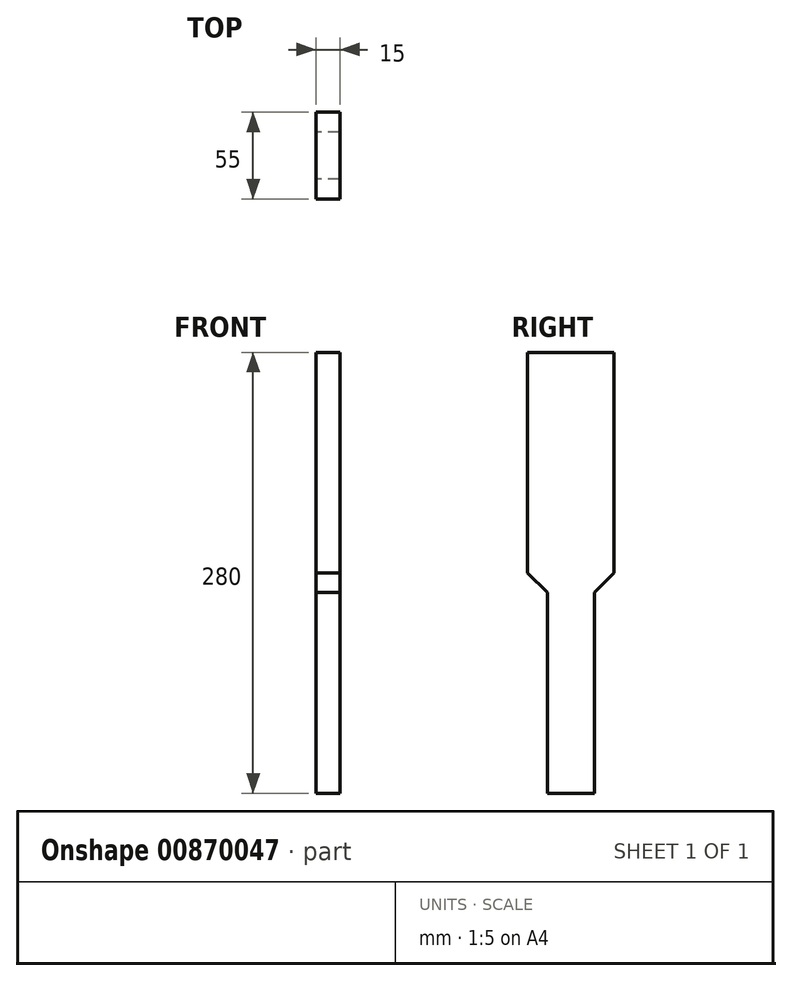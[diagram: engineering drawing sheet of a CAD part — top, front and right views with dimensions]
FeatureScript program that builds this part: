
annotation { "Feature Type Name" : "Feature", "Feature Type Description" : "" }
export const myFeature = defineFeature(function(context is Context, id is Id, definition is map)
    precondition{}
    {
        {
            var Q0;
            Q0=qCreatedBy(makeId("Right.planeOp"),FACE);
            var sketch = newSketch(context, id + "F0", { "sketchPlane" : qUnion([Q0])});
            skLineSegment(sketch, "E0", {"start": v(0, 140) * mm, "end": v(0, 0) * mm});
            skLineSegment(sketch, "E1", {"start": v(55, 0) * mm, "end": v(55, 140) * mm});
            skLineSegment(sketch, "E2", {"start": v(55, 140) * mm, "end": v(0, 140) * mm});
            skLineSegment(sketch, "E3", {"start": v(0, 0) * mm, "end": v(12.5, -12.5) * mm});
            skLineSegment(sketch, "E4", {"start": v(55, 0) * mm, "end": v(42.5, -12.5) * mm});
            skLineSegment(sketch, "E5", {"start": v(12.5, -12.5) * mm, "end": v(12.5, -140) * mm});
            skLineSegment(sketch, "E6", {"start": v(12.5, -140) * mm, "end": v(42.5, -140) * mm});
            skLineSegment(sketch, "E7", {"start": v(42.5, -140) * mm, "end": v(42.5, -12.5) * mm});
            skLineSegment(sketch, "E8", {"start": v(12.5, -12.5) * mm, "end": v(42.5, -12.5) * mm, "construction": true});
            skLineSegment(sketch, "E9", {"start": v(0, 0) * mm, "end": v(55, 0) * mm, "construction": true});
            skSolve(sketch);
        }
        {
            var Q0;
            Q0 = qSketchRegion(id + "F0", true);
            extrude(context, id + "F1", {"entities" : qUnion([Q0]), "depth" : 15 * mm, "offsetDistance" : 25 * mm});
        }
    });
